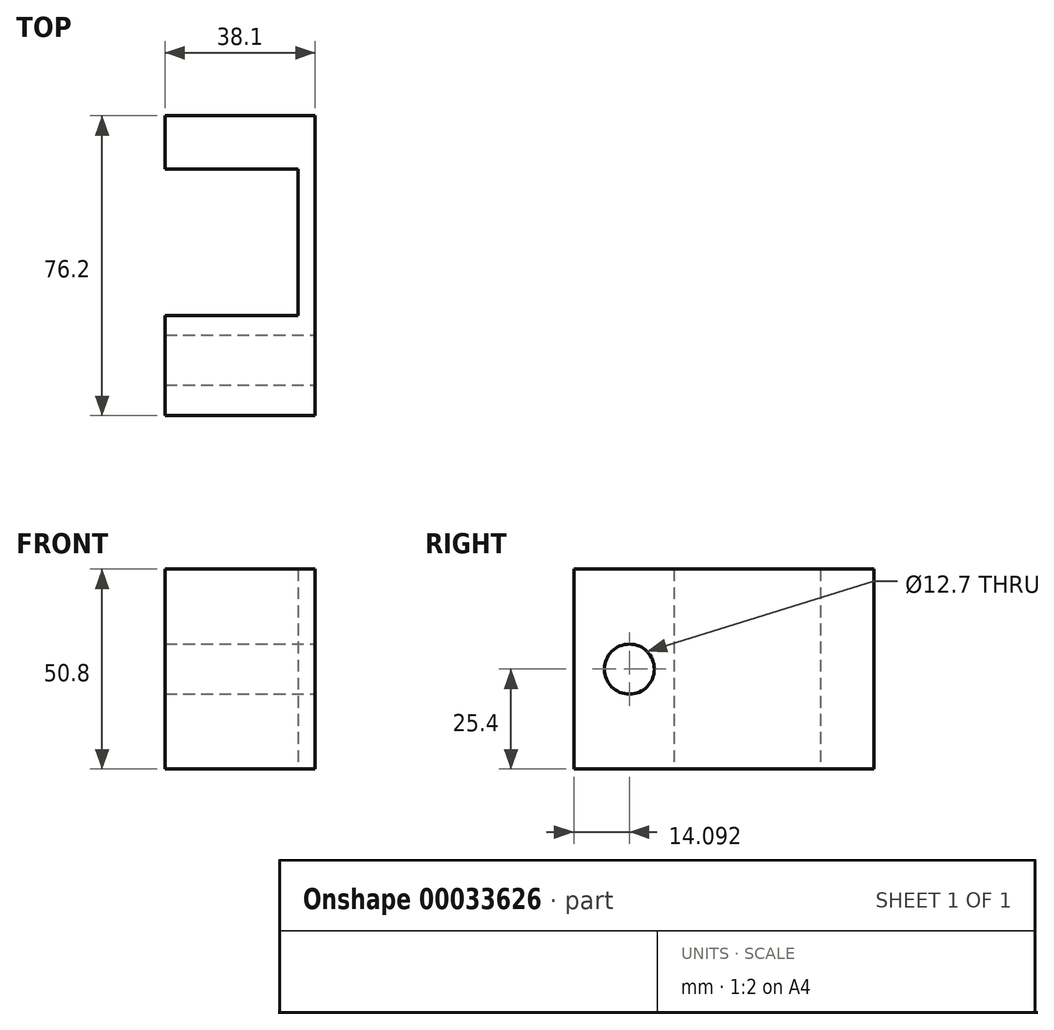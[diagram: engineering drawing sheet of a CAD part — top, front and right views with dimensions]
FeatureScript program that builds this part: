
annotation { "Feature Type Name" : "Feature", "Feature Type Description" : "" }
export const myFeature = defineFeature(function(context is Context, id is Id, definition is map)
    precondition{}
    {
        {
            var Q0;
            Q0=qCreatedBy(makeId("Top.planeOp"),FACE);
            var sketch = newSketch(context, id + "F0", { "sketchPlane" : qUnion([Q0])});
            skLineSegment(sketch, "E0.bottom", {"start": v(-0.62, 0) * mm, "end": v(37.48, 0) * mm});
            skLineSegment(sketch, "E0.top", {"start": v(-0.62, 76.2) * mm, "end": v(37.48, 76.2) * mm});
            skLineSegment(sketch, "E0.left", {"start": v(-0.62, 0) * mm, "end": v(-0.62, 76.2) * mm});
            skLineSegment(sketch, "E0.right", {"start": v(37.48, 0) * mm, "end": v(37.48, 76.2) * mm});
            skLineSegment(sketch, "E1.bottom", {"start": v(-0.62, 62.66) * mm, "end": v(33.23, 62.66) * mm});
            skLineSegment(sketch, "E1.top", {"start": v(-0.62, 25.4) * mm, "end": v(33.23, 25.4) * mm});
            skLineSegment(sketch, "E1.left", {"start": v(-0.62, 62.66) * mm, "end": v(-0.62, 25.4) * mm});
            skLineSegment(sketch, "E1.right", {"start": v(33.23, 62.66) * mm, "end": v(33.23, 25.4) * mm});
            skSolve(sketch);
        }
        {
            var Q0;
            {var subQ5=sQuery(id+"F0.wireOp",EDGE,"E0.bottom");Q0=makeQuery(id+"F0.imprint","IMPRINT",FACE,{"disambiguationData":[TD([[makeQuery(id+"F0.imprint","IMPRINT",EDGE,{"derivedFrom":subQ5}),1.0]])]});}
            extrude(context, id + "F1", {"entities" : qUnion([Q0]), "depth" : 50.8 * mm});
        }
        {
            var Q0;
            Q0=makeQuery(id+"F1.opExtrude","SWEPT_FACE",FACE,{"disambiguationData":[OSD([sQuery(id+"F0.wireOp",EDGE,"E0.right")])]});
            var sketch = newSketch(context, id + "F2", { "sketchPlane" : qUnion([Q0])});
            skCircle(sketch, "E2", {"center": v(14.1, 25.4) * mm, "radius": 6.35 * mm});
            skPoint(sketch, "E2.centerSnap0", {"position": v(0, 25.4) * mm});
            skSolve(sketch);
        }
        {
            var Q0;
            Q0=makeQuery(id+"F2.imprint","IMPRINT",FACE,{"disambiguationData":[TD([[makeQuery(id+"F2.imprint","IMPRINT",EDGE,{"derivedFrom":sQuery(id+"F2.wireOp",EDGE,"E2")}),1.0]])]});
            extrude(context, id + "F3", {"entities" : qUnion([Q0]), "operationType" : NewBodyOperationType.REMOVE, "oppositeDirection" : true, "depth" : 50.8 * mm});
        }
    });
